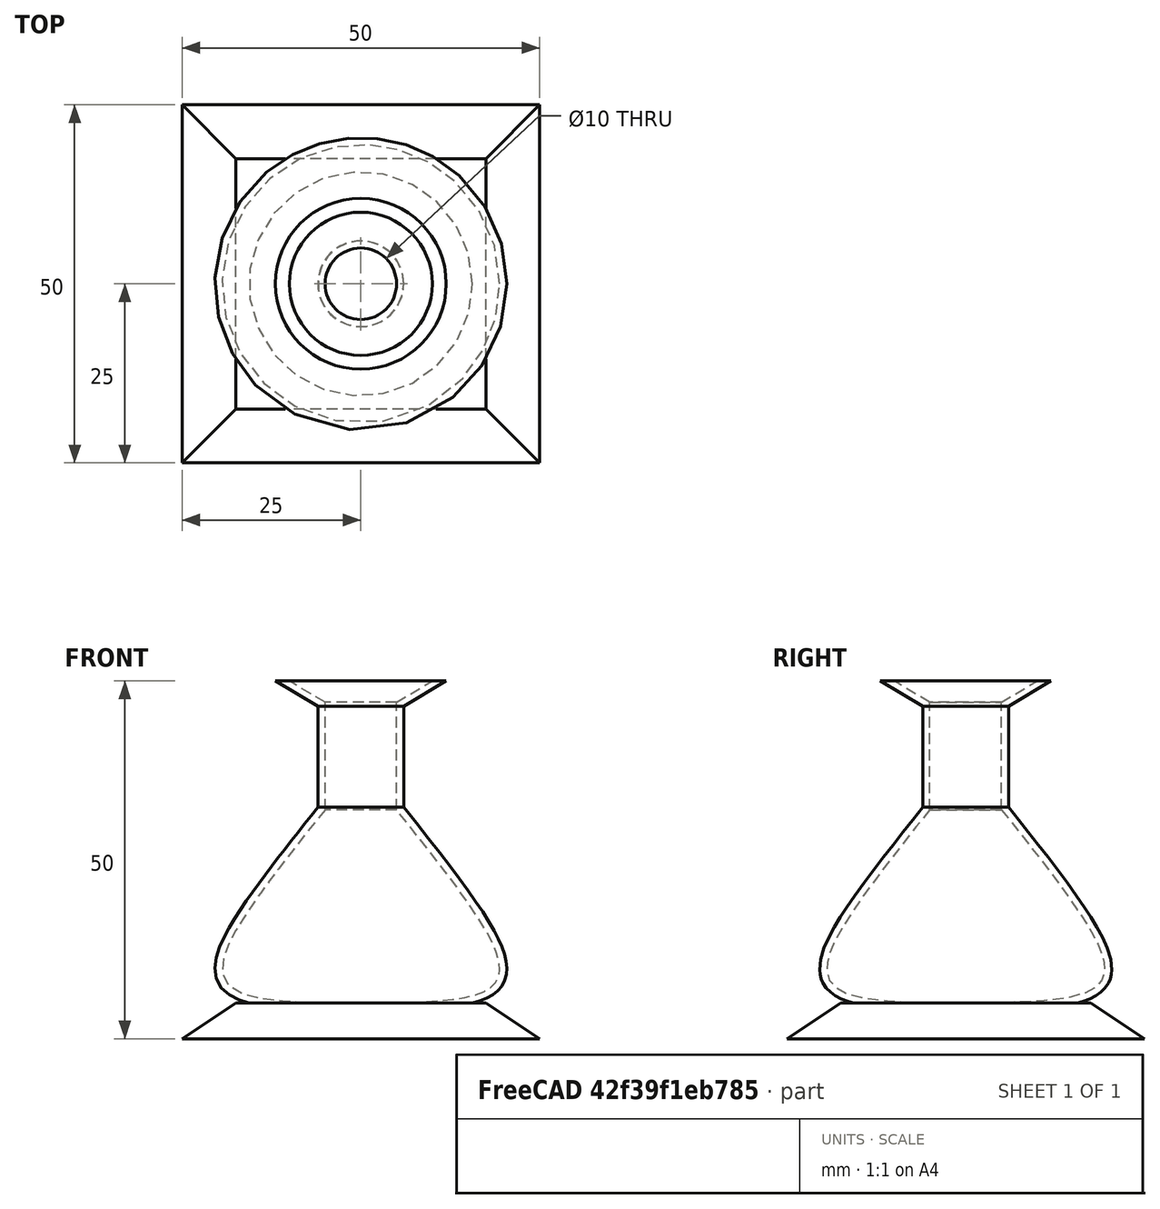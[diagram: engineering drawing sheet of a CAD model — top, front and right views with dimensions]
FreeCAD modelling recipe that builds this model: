
FCSTD DOCUMENT  (FreeCAD 0.18R4 (GitTag))
Label: l 10 q3
License: All rights reserved
LicenseURL: http://en.wikipedia.org/wiki/All_rights_reserved
objects: Sketcher::SketchObject×4, PartDesign::Pocket×2, PartDesign::Revolution×1, PartDesign::Thickness×1, PartDesign::Plane×1, PartDesign::Pad×1, PartDesign::Body×1
note: 15 computed .brp shape members not serialized (recipe doc carries the construction recipe); baked Part::Feature solids carry a one-line shape summary decoded from their .brp

FEATURE [Sketcher::SketchObject] Sketch
  MapMode = 5
  Placement = pos=(0,0,0) rot=(1,0,0;1.5708rad)
  Support = -> [XZ_Plane]
  sketch-geometry (11):
    g0: LineSegment StartX=5 StartY=27 StartZ=0 EndX=5 EndY=42 EndZ=0
    g1: LineSegment StartX=5 StartY=42 StartZ=0 EndX=10 EndY=45 EndZ=0
    g2: LineSegment StartX=10 StartY=45 StartZ=0 EndX=0 EndY=45 EndZ=0
    g3-g6: Circle [constr] x4 (B-spline internal-alignment scaffolding for g7; pole/knot coordinates omitted)
    g7: BSplineCurve PolesCount=4 KnotsCount=2 Degree=3 IsPeriodic=0
    g8: GeomPoint [constr] X=0 Y=0 Z=0
    g9: GeomPoint [constr] X=5 Y=27 Z=0
    g10: LineSegment StartX=1e-16 StartY=45 StartZ=0 EndX=0 EndY=0 EndZ=0
  constraints (25):
    c: Coincident(g2,g1)
    c: Coincident(g0,g1)
    c: Vertical(g0)
    c: Horizontal(g2)
    c: Distance(g2) = 10
    c: DistanceY(g0,g1) = 3
    c: DistanceX(g2,g0) = 5
    c: DistanceY(g0,g0) = 15
    c: Radius(g3) = 3
    c: Equal(g3,g4)
    c: Equal(g3,g5)
    c: Equal(g3,g6)
    c: InternalAlignment(g3-g6 -> g7) x4
    c: InternalAlignment(g8,g7)
    c: InternalAlignment(g9,g7)
    c: DistanceY(g7,g4) = 0
    c: DistanceX(g7,g4) = 25
    c: DistanceX(g5,g4) = 0
    c: DistanceY(g4,g5) = 2
    c: DistanceX(g7,g7) = -5
    c: DistanceY(g7,g7) = 27
    c: Coincident(g7,g0)
    c: Coincident(g10,g2)
    c: Coincident(g10,g7)
    c: Coincident(g7,g-1)
FEATURE [PartDesign::Revolution] Revolution
  Angle = 360
  Axis = (0,2e-16,1)
  Base = (0,0,0)
  Placement = pos=(0,0,0) rot=(1,0,0;1.5708rad)
  Profile = -> Sketch
  ReferenceAxis = -> Sketch [V_Axis]
  Reversed = true
FEATURE [PartDesign::Thickness] Thickness
  Base = -> Revolution [Face3]
  BaseFeature = -> Revolution
  Join = 0
  Mode = 0
  Value = 1
FEATURE [PartDesign::Plane] DatumPlane
  AttachmentOffset = pos=(0,0,-45) rot=(0,0,1;0rad)
  Length = 60
  MapMode = 5
  Placement = pos=(0,0,-7.1e-15) rot=(0,0,1;0rad)
  ResizeMode = 0
  Support = -> [Thickness]
  Width = 60
FEATURE [Sketcher::SketchObject] Sketch001
  MapMode = 5
  Placement = pos=(0,0,-7.1e-15) rot=(0,0,1;0rad)
  Support = -> [DatumPlane]
  sketch-geometry (4):
    g0: LineSegment StartX=-25 StartY=25 StartZ=0 EndX=25 EndY=25 EndZ=0
    g1: LineSegment StartX=25 StartY=25 StartZ=0 EndX=25 EndY=-25 EndZ=0
    g2: LineSegment StartX=25 StartY=-25 StartZ=0 EndX=-25 EndY=-25 EndZ=0
    g3: LineSegment StartX=-25 StartY=-25 StartZ=0 EndX=-25 EndY=25 EndZ=0
  constraints (12):
    c: Coincident(g0,g1)
    c: Coincident(g1,g2)
    c: Coincident(g2,g3)
    c: Coincident(g3,g0)
    c: Horizontal(g0)
    c: Horizontal(g2)
    c: Vertical(g1)
    c: Vertical(g3)
    c: Distance(g1) = 50
    c: Distance(g0) = 50
    c: DistanceX(g-1,g0) = 25
    c: DistanceY(g-1,g0) = 25
FEATURE [PartDesign::Pad] Pad
  BaseFeature = -> Thickness
  Length = 5
  Length2 = 100
  Profile = -> Sketch001
  Reversed = true
  Type = 0
FEATURE [Sketcher::SketchObject] Sketch002
  ExternalGeometry = -> [Pad]
  MapMode = 5
  Placement = pos=(25,0,0) rot=(0.57735,0.57735,0.57735;2.0944rad)
  Support = -> [Pad]
  sketch-geometry (6):
    g0: LineSegment StartX=-25 StartY=-5 StartZ=0 EndX=-25 EndY=9.8e-15 EndZ=0
    g1: LineSegment StartX=-25 StartY=9.8e-15 StartZ=0 EndX=-17.5 EndY=9.8e-15 EndZ=0
    g2: LineSegment StartX=-17.5 StartY=9.8e-15 StartZ=0 EndX=-25 EndY=-5 EndZ=0
    g3: LineSegment StartX=25 StartY=-5 StartZ=0 EndX=17.5 EndY=-2.4e-14 EndZ=0
    g4: LineSegment StartX=17.5 StartY=-2.38e-14 StartZ=0 EndX=25 EndY=-2.38e-14 EndZ=0
    g5: LineSegment StartX=25 StartY=-2.38e-14 StartZ=0 EndX=25 EndY=-5 EndZ=0
  constraints (15):
    c: Coincident(g0,g1)
    c: Coincident(g1,g2)
    c: Coincident(g2,g0)
    c: Coincident(g0,g-4)
    c: Vertical(g0)
    c: Horizontal(g1)
    c: Distance(g0) = 5
    c: Distance(g1) = 7.5
    c: Coincident(g3,g4)
    c: Coincident(g4,g5)
    c: Coincident(g4,g-3)
    c: Coincident(g5,g-3)
    c: Coincident(g3,g5)
    c: Horizontal(g4)
    c: Distance(g4) = 7.5
FEATURE [Sketcher::SketchObject] Sketch003
  ExternalGeometry = -> [Pad]
  MapMode = 5
  Placement = pos=(0,-25,1.67e-14) rot=(1,0,0;1.5708rad)
  Support = -> [Pad]
  sketch-geometry (6):
    g0: LineSegment StartX=-25 StartY=-5 StartZ=0 EndX=-17.5 EndY=-7.1e-15 EndZ=0
    g1: LineSegment StartX=-17.5 StartY=-7.1e-15 StartZ=0 EndX=-25 EndY=-7.1e-15 EndZ=0
    g2: LineSegment StartX=-25 StartY=-7.1e-15 StartZ=0 EndX=-25 EndY=-5 EndZ=0
    g3: LineSegment StartX=25 StartY=-5 StartZ=0 EndX=17.5 EndY=-7.1e-15 EndZ=0
    g4: LineSegment StartX=17.5 StartY=-7.1e-15 StartZ=0 EndX=25 EndY=-7.1e-15 EndZ=0
    g5: LineSegment StartX=25 StartY=-7.1e-15 StartZ=0 EndX=25 EndY=-5 EndZ=0
  constraints (14):
    c: Coincident(g0,g1)
    c: Coincident(g1,g2)
    c: Coincident(g2,g-3)
    c: Coincident(g1,g-3)
    c: Coincident(g0,g2)
    c: Horizontal(g1)
    c: Distance(g1) = 7.5
    c: Coincident(g3,g4)
    c: Coincident(g4,g5)
    c: Coincident(g3,g-4)
    c: Coincident(g5,g3)
    c: Coincident(g4,g-4)
    c: Horizontal(g4)
    c: Distance(g4) = 7.5
FEATURE [PartDesign::Pocket] Pocket
  BaseFeature = -> Pad
  Length = 50
  Length2 = 100
  Profile = -> Sketch002
  Type = 0
FEATURE [PartDesign::Pocket] Pocket001
  BaseFeature = -> Pocket
  Length = 50
  Length2 = 100
  Profile = -> Sketch003
  Type = 0
FEATURE [PartDesign::Body] Body
  Group = -> [Sketch,Revolution,Thickness,DatumPlane,Sketch001,Pad,Sketch002,Sketch003,Pocket,Pocket001]
  Origin = -> Origin
  Tip = -> Pocket001
